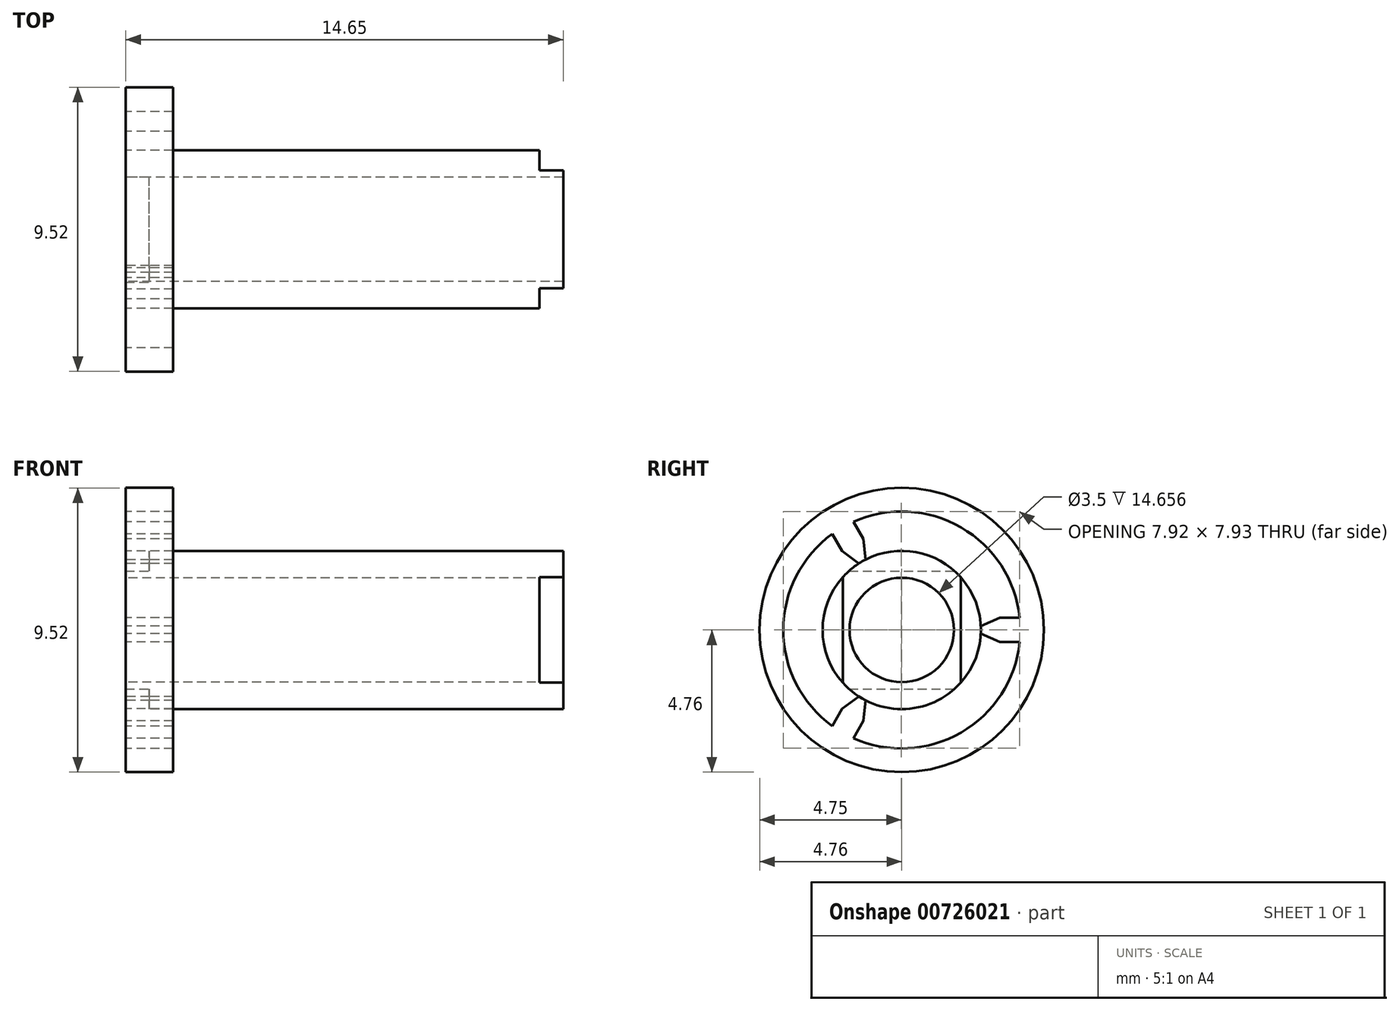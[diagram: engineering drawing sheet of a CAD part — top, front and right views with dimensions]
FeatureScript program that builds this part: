
annotation { "Feature Type Name" : "Feature", "Feature Type Description" : "" }
export const myFeature = defineFeature(function(context is Context, id is Id, definition is map)
    precondition{}
    {
        {
            var Q0;
            Q0=qCreatedBy(makeId("Right.planeOp"),FACE);
            var sketch = newSketch(context, id + "F0", { "sketchPlane" : qUnion([Q0])});
            skCircle(sketch, "E0", {"center": v(0, 0) * mm, "radius": 2.65 * mm});
            skCircle(sketch, "E1", {"center": v(0, 0) * mm, "radius": 1.75 * mm});
            skLineSegment(sketch, "E2.bottom", {"start": v(-1.77, -1.98) * mm, "end": v(1.77, -1.98) * mm});
            skLineSegment(sketch, "E2.top", {"start": v(-1.77, 1.98) * mm, "end": v(1.77, 1.98) * mm});
            skLineSegment(sketch, "E2.left", {"start": v(-1.77, -1.98) * mm, "end": v(-1.77, 1.98) * mm});
            skLineSegment(sketch, "E2.right", {"start": v(1.77, -1.98) * mm, "end": v(1.77, 1.98) * mm});
            skCircle(sketch, "E3", {"center": v(0, 0) * mm, "radius": 4.76 * mm});
            skCircle(sketch, "E4", {"center": v(0, 0) * mm, "radius": 3.97 * mm});
            skLineSegment(sketch, "E5", {"start": v(3.29, 0.4) * mm, "end": v(3.95, 0.4) * mm});
            skLineSegment(sketch, "E6", {"start": v(3.29, 0.4) * mm, "end": v(2.65, 0.13) * mm});
            skLineSegment(sketch, "E7", {"start": v(0, 0) * mm, "end": v(1.75, 0) * mm, "construction": true});
            skPoint(sketch, "E7.endSnap0", {"position": v(1.77, 0) * mm});
            skPoint(sketch, "E8.orphan", {"position": v(2.62, 0.4) * mm});
            skLineSegment(sketch, "E9.MirrorCS", {"start": v(3.29, -0.4) * mm, "end": v(2.65, -0.13) * mm});
            skLineSegment(sketch, "E10.MirrorCS", {"start": v(3.29, -0.4) * mm, "end": v(3.95, -0.4) * mm});
            skLineSegment(sketch, "E11.1.0", {"start": v(-2, 2.64) * mm, "end": v(-2.33, 3.22) * mm});
            skLineSegment(sketch, "E11.1.1", {"start": v(-2, 2.64) * mm, "end": v(-1.43, 2.23) * mm});
            skLineSegment(sketch, "E11.1.2", {"start": v(-1.3, 3.05) * mm, "end": v(-1.21, 2.36) * mm});
            skLineSegment(sketch, "E11.1.3", {"start": v(-1.3, 3.05) * mm, "end": v(-1.62, 3.62) * mm});
            skLineSegment(sketch, "E11.2.0", {"start": v(-1.3, -3.05) * mm, "end": v(-1.62, -3.62) * mm});
            skLineSegment(sketch, "E11.2.1", {"start": v(-1.3, -3.05) * mm, "end": v(-1.21, -2.36) * mm});
            skLineSegment(sketch, "E11.2.2", {"start": v(-2, -2.64) * mm, "end": v(-1.43, -2.23) * mm});
            skLineSegment(sketch, "E11.2.3", {"start": v(-2, -2.64) * mm, "end": v(-2.33, -3.22) * mm});
            skSolve(sketch);
        }
        {
            var Q0;
            {var subQ0=sQuery(id+"F0.wireOp",EDGE,"E2.left");var subQ4=sQuery(id+"F0.wireOp",EDGE,"E1");var subQ5=makeQuery(id+"F0.imprint","INTERSECT",VERTEX,{"disambiguationData":[OD(0.0)],"derivedFrom":[subQ4,subQ0]});Q0=makeQuery(id+"F0.imprint","IMPRINT",FACE,{"disambiguationData":[TD([[makeQuery(id+"F0.imprint","IMPRINT",EDGE,{"disambiguationData":[TD([[subQ5,-1.0]])],"derivedFrom":subQ4}),-1.0]])]});}
            var Q1;
            {var subQ5=sQuery(id+"F0.wireOp",EDGE,"E2.top");Q1=makeQuery(id+"F0.imprint","IMPRINT",FACE,{"disambiguationData":[TD([[makeQuery(id+"F0.imprint","IMPRINT",EDGE,{"derivedFrom":subQ5}),-1.0]])]});}
            var Q2;
            {var subQ0=sQuery(id+"F0.wireOp",EDGE,"E2.top");Q2=makeQuery(id+"F0.imprint","IMPRINT",FACE,{"disambiguationData":[TD([[makeQuery(id+"F0.imprint","IMPRINT",EDGE,{"derivedFrom":subQ0}),1.0]])]});}
            var Q3;
            {var subQ0=sQuery(id+"F0.wireOp",EDGE,"E2.right");var subQ4=sQuery(id+"F0.wireOp",EDGE,"E1");var subQ6=makeQuery(id+"F0.imprint","INTERSECT",VERTEX,{"disambiguationData":[OD(0.0)],"derivedFrom":[subQ4,subQ0]});Q3=makeQuery(id+"F0.imprint","IMPRINT",FACE,{"disambiguationData":[TD([[makeQuery(id+"F0.imprint","IMPRINT",EDGE,{"disambiguationData":[TD([[subQ6,1.0]])],"derivedFrom":subQ4}),-1.0]])]});}
            var Q4;
            {var subQ5=sQuery(id+"F0.wireOp",EDGE,"E2.bottom");Q4=makeQuery(id+"F0.imprint","IMPRINT",FACE,{"disambiguationData":[TD([[makeQuery(id+"F0.imprint","IMPRINT",EDGE,{"derivedFrom":subQ5}),1.0]])]});}
            var Q5;
            {var subQ0=sQuery(id+"F0.wireOp",EDGE,"E2.bottom");Q5=makeQuery(id+"F0.imprint","IMPRINT",FACE,{"disambiguationData":[TD([[makeQuery(id+"F0.imprint","IMPRINT",EDGE,{"derivedFrom":subQ0}),-1.0]])]});}
            var Q6;
            {var subQ0=sQuery(id+"F0.wireOp",EDGE,"E2.right");Q6=makeQuery(id+"F0.imprint","IMPRINT",FACE,{"disambiguationData":[TD([[makeQuery(id+"F0.imprint","IMPRINT",EDGE,{"derivedFrom":subQ0}),-1.0]])]});}
            var Q7;
            {var subQ0=sQuery(id+"F0.wireOp",EDGE,"E2.left");Q7=makeQuery(id+"F0.imprint","IMPRINT",FACE,{"disambiguationData":[TD([[makeQuery(id+"F0.imprint","IMPRINT",EDGE,{"derivedFrom":subQ0}),1.0]])]});}
            extrude(context, id + "F1", {"entities" : qUnion([Q0, Q1, Q2, Q3, Q4, Q5, Q6, Q7]), "depth" : 13.07 * mm, "offsetDistance" : 25.4 * mm});
        }
        {
            var Q0;
            {var subQ5=sQuery(id+"F0.wireOp",EDGE,"E2.top");Q0=makeQuery(id+"F0.imprint","IMPRINT",FACE,{"disambiguationData":[TD([[makeQuery(id+"F0.imprint","IMPRINT",EDGE,{"derivedFrom":subQ5}),-1.0]])]});}
            var Q1;
            {var subQ5=sQuery(id+"F0.wireOp",EDGE,"E2.bottom");Q1=makeQuery(id+"F0.imprint","IMPRINT",FACE,{"disambiguationData":[TD([[makeQuery(id+"F0.imprint","IMPRINT",EDGE,{"derivedFrom":subQ5}),1.0]])]});}
            var Q2;
            {var subQ0=sQuery(id+"F0.wireOp",EDGE,"E2.left");Q2=makeQuery(id+"F0.imprint","IMPRINT",FACE,{"disambiguationData":[TD([[makeQuery(id+"F0.imprint","IMPRINT",EDGE,{"derivedFrom":subQ0}),1.0]])]});}
            var Q3;
            {var subQ0=sQuery(id+"F0.wireOp",EDGE,"E2.right");Q3=makeQuery(id+"F0.imprint","IMPRINT",FACE,{"disambiguationData":[TD([[makeQuery(id+"F0.imprint","IMPRINT",EDGE,{"derivedFrom":subQ0}),-1.0]])]});}
            extrude(context, id + "F2", {"entities" : qUnion([Q0, Q1, Q2, Q3]), "operationType" : NewBodyOperationType.ADD, "oppositeDirection" : true, "depth" : 0.8 * mm, "offsetDistance" : 25.4 * mm});
        }
        {
            var Q0;
            Q0=makeQuery(id+"F1.opExtrude","CAP_FACE",FACE,{"disambiguationData":[OSD([sQuery(id+"F0.wireOp",EDGE,"E0"),sQuery(id+"F0.wireOp",EDGE,"E1")])],"isStart":false});
            var sketch = newSketch(context, id + "F3", { "sketchPlane" : qUnion([Q0])});
            skLineSegment(sketch, "E12.bottom", {"start": v(-1.98, 1.77) * mm, "end": v(1.98, 1.77) * mm});
            skLineSegment(sketch, "E12.top", {"start": v(-1.98, -1.77) * mm, "end": v(1.98, -1.77) * mm});
            skLineSegment(sketch, "E12.left", {"start": v(-1.98, 1.77) * mm, "end": v(-1.98, -1.77) * mm});
            skLineSegment(sketch, "E12.right", {"start": v(1.98, 1.77) * mm, "end": v(1.98, -1.77) * mm});
            skPoint(sketch, "E12.middle", {"position": v(0, 0) * mm});
            skSolve(sketch);
        }
        {
            var Q0;
            {var subQ0=sQuery(id+"F3.wireOp",EDGE,"E12.left");Q0=makeQuery(id+"F3.imprint","IMPRINT",FACE,{"disambiguationData":[TD([[makeQuery(id+"F3.imprint","IMPRINT",EDGE,{"derivedFrom":subQ0}),1.0]])]});}
            var Q1;
            {var subQ0=sQuery(id+"F3.wireOp",EDGE,"E12.right");Q1=makeQuery(id+"F3.imprint","IMPRINT",FACE,{"disambiguationData":[TD([[makeQuery(id+"F3.imprint","IMPRINT",EDGE,{"derivedFrom":subQ0}),-1.0]])]});}
            var Q2;
            {var subQ0=sQuery(id+"F3.wireOp",EDGE,"E12.bottom");Q2=makeQuery(id+"F3.imprint","IMPRINT",FACE,{"disambiguationData":[TD([[makeQuery(id+"F3.imprint","IMPRINT",EDGE,{"derivedFrom":subQ0}),1.0]])]});}
            var Q3;
            {var subQ0=sQuery(id+"F3.wireOp",EDGE,"E12.top");Q3=makeQuery(id+"F3.imprint","IMPRINT",FACE,{"disambiguationData":[TD([[makeQuery(id+"F3.imprint","IMPRINT",EDGE,{"derivedFrom":subQ0}),-1.0]])]});}
            extrude(context, id + "F4", {"entities" : qUnion([Q0, Q1, Q2, Q3]), "operationType" : NewBodyOperationType.ADD, "depth" : 0.8 * mm, "offsetDistance" : 25.4 * mm});
        }
        {
            var Q0;
            Q0=makeQuery(id+"F0.imprint","IMPRINT",FACE,{"disambiguationData":[TD([[makeQuery(id+"F0.imprint","IMPRINT",EDGE,{"derivedFrom":sQuery(id+"F0.wireOp",EDGE,"E3")}),1.0]])]});
            var Q1;
            {var subQ0=sQuery(id+"F0.wireOp",EDGE,"FdiQmzWI-4J4r-O7IK-cBai-K4ANbvjLphNO");Q1=makeQuery(id+"F0.imprint","IMPRINT",FACE,{"disambiguationData":[TD([[makeQuery(id+"F0.imprint","IMPRINT",EDGE,{"derivedFrom":subQ0}),1.0]])]});}
            var Q2;
            {var subQ0=sQuery(id+"F0.wireOp",EDGE,"cdf957fa-af96-419c-97ca-f235cde1413e.1.0");Q2=makeQuery(id+"F0.imprint","IMPRINT",FACE,{"disambiguationData":[TD([[makeQuery(id+"F0.imprint","IMPRINT",EDGE,{"derivedFrom":subQ0}),-1.0]])]});}
            var Q3;
            {var subQ0=sQuery(id+"F0.wireOp",EDGE,"cdf957fa-af96-419c-97ca-f235cde1413e.2.0");Q3=makeQuery(id+"F0.imprint","IMPRINT",FACE,{"disambiguationData":[TD([[makeQuery(id+"F0.imprint","IMPRINT",EDGE,{"derivedFrom":subQ0}),-1.0]])]});}
            var Q4;
            {var subQ1=sQuery(id+"F0.wireOp",EDGE,"E5");Q4=makeQuery(id+"F0.imprint","IMPRINT",FACE,{"disambiguationData":[TD([[makeQuery(id+"F0.imprint","IMPRINT",EDGE,{"derivedFrom":subQ1}),-1.0]])]});}
            var Q5;
            {var subQ1=sQuery(id+"F0.wireOp",EDGE,"E11.1.0");Q5=makeQuery(id+"F0.imprint","IMPRINT",FACE,{"disambiguationData":[TD([[makeQuery(id+"F0.imprint","IMPRINT",EDGE,{"derivedFrom":subQ1}),-1.0]])]});}
            var Q6;
            {var subQ3=sQuery(id+"F0.wireOp",EDGE,"E11.2.0");Q6=makeQuery(id+"F0.imprint","IMPRINT",FACE,{"disambiguationData":[TD([[makeQuery(id+"F0.imprint","IMPRINT",EDGE,{"derivedFrom":subQ3}),-1.0]])]});}
            extrude(context, id + "F5", {"entities" : qUnion([Q0, Q1, Q2, Q3, Q4, Q5, Q6]), "operationType" : NewBodyOperationType.ADD, "depth" : 1.59 * mm, "offsetDistance" : 25.4 * mm, "symmetric" : true});
        }
    });
